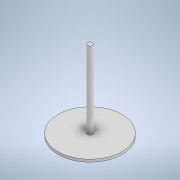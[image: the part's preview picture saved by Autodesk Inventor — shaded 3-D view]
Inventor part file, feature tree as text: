
AUTODESK INVENTOR PART (.ipt)
format: ipt  version: 2021 (Build 250183000, 183)  size: 103,424 bytes
history: native  units: in
note: dims shown in document units (in); Inventor stores cm internally (conversion verified against a paired STEP export)
features: extrude x2, sketch x2
ambient origin geometry x8: Origin, YZ Plane, XZ Plane, XY Plane, X Axis, Y Axis, Z Axis, Center Point
bodies: Solid1 (feature_tree)
feature tree (4):
  extrude  "Extrusion1"  Depth=2.0in
  extrude  "Extrusion2"  Depth=30.0in TaperAngle=0.0deg
  sketch  "Sketch1"  dims[d0=25.0in d1=2.0in]
  sketch  "Sketch2"  dims[d2=1.0in d3=0.0in d4=30.0in d5=0.0in d6=1.0in d7=0.0in]
